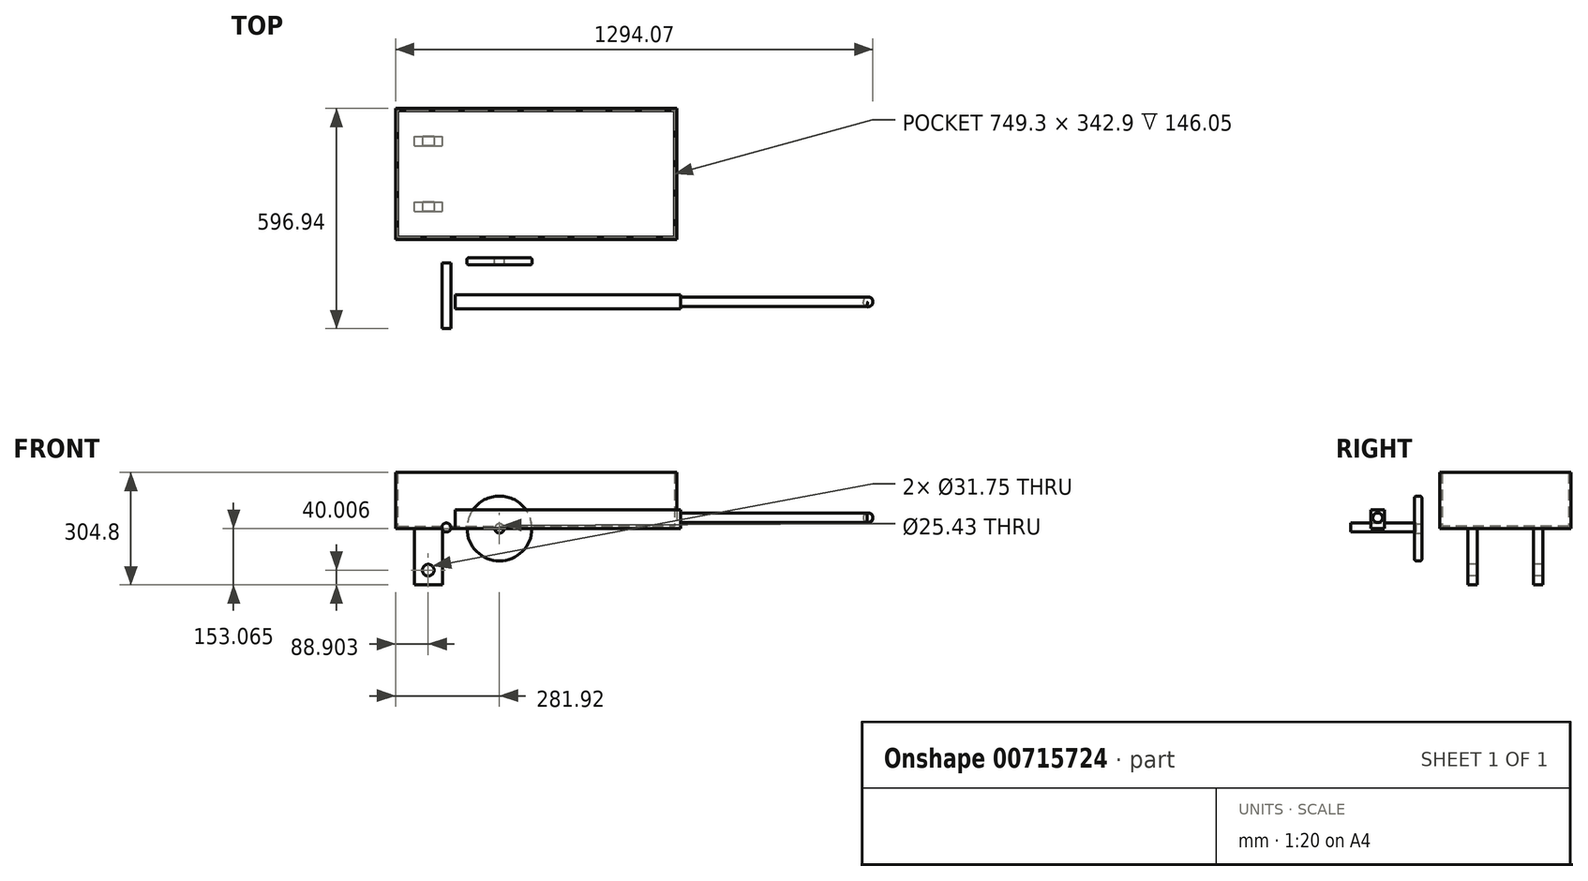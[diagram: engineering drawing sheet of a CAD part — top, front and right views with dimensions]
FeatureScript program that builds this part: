
annotation { "Feature Type Name" : "Feature", "Feature Type Description" : "" }
export const myFeature = defineFeature(function(context is Context, id is Id, definition is map)
    precondition{}
    {
        {
            var Q0;
            Q0=qCreatedBy(makeId("Top.planeOp"),FACE);
            var sketch = newSketch(context, id + "F0", { "sketchPlane" : qUnion([Q0])});
            skLineSegment(sketch, "E0.bottom", {"start": v(0, -5.26) * mm, "end": v(75.35, -5.26) * mm});
            skLineSegment(sketch, "E0.top", {"start": v(0, 14.29) * mm, "end": v(75.35, 14.29) * mm});
            skLineSegment(sketch, "E0.left", {"start": v(0, -5.26) * mm, "end": v(0, 14.29) * mm});
            skLineSegment(sketch, "E0.right", {"start": v(75.35, -5.26) * mm, "end": v(75.35, 14.29) * mm});
            skArc(sketch, "E1", {"start": v(75.35, -5.26) * mm, "mid": v(85.12, 4.51) * mm, "end": v(75.35, 14.29) * mm});
            skSolve(sketch);
        }
        {
            var Q0;
            Q0=qCreatedBy(makeId("Front.planeOp"),FACE);
            var sketch = newSketch(context, id + "F1", { "sketchPlane" : qUnion([Q0])});
            skCircle(sketch, "E2", {"center": v(-12.7, 0.66) * mm, "radius": 12.72 * mm});
            skPoint(sketch, "E2.first.point", {"position": v(0, 0) * mm});
            skPoint(sketch, "E2.second.point", {"position": v(-25.4, 0) * mm});
            skPoint(sketch, "E2.third.point", {"position": v(-23.5, -6.04) * mm});
            skSolve(sketch);
        }
        {
            var Q0;
            Q0=makeQuery(id+"F0.imprint","IMPRINT",FACE,{"disambiguationData":[TD([[makeQuery(id+"F0.imprint","IMPRINT",EDGE,{"derivedFrom":sQuery(id+"F0.wireOp",EDGE,"E0.bottom")}),1.0]])]});
            var Q1;
            Q1=sQuery(id+"F1.wireOp",EDGE,"E2");
            revolve(context, id + "F2", {"surfaceOperationType" : NewSurfaceOperationType.NEW, "entities" : qUnion([Q0]), "axis" : qUnion([Q1]), "revolveType" : RevolveType.FULL});
        }
        {
            var Q0;
            Q0=makeQuery(id+"F2.opRevolve","SWEPT_EDGE",EDGE,{"disambiguationData":[OSD([sQuery(id+"F0.wireOp",EDGE,"E0.top"),sQuery(id+"F0.wireOp",EDGE,"E0.right"),sQuery(id+"F0.wireOp",EDGE,"E1")])]});
            var Q1;
            Q1=makeQuery(id+"F2.opRevolve","SWEPT_EDGE",EDGE,{"disambiguationData":[OSD([sQuery(id+"F0.wireOp",EDGE,"E0.bottom"),sQuery(id+"F0.wireOp",EDGE,"E0.right"),sQuery(id+"F0.wireOp",EDGE,"E1")])]});
            fillet(context, id + "F3", {"entities" : qUnion([Q0, Q1]), "radius" : 5.08 * mm, "tangentPropagation" : true, "allowEdgeOverflow" : false});
        }
        {
            var Q0;
            Q0=qCreatedBy(makeId("Front.planeOp"),FACE);
            var sketch = newSketch(context, id + "F4", { "sketchPlane" : qUnion([Q0])});
            skCircle(sketch, "E3", {"center": v(-156.6, 3.33) * mm, "radius": 12.2 * mm});
            skSolve(sketch);
        }
        {
            var Q0;
            Q0=makeQuery(id+"F4.imprint","IMPRINT",FACE,{"disambiguationData":[TD([[makeQuery(id+"F4.imprint","IMPRINT",EDGE,{"derivedFrom":sQuery(id+"F4.wireOp",EDGE,"E3")}),1.0]])]});
            extrude(context, id + "F5", {"entities" : qUnion([Q0]), "depth" : 177.8 * mm, "offsetDistance" : 25.4 * mm});
        }
        {
            var Q0;
            Q0=qCreatedBy(makeId("Top.planeOp"),FACE);
            var sketch = newSketch(context, id + "F6", { "sketchPlane" : qUnion([Q0])});
            skLineSegment(sketch, "E4.bottom", {"start": v(-89.13, -56.6) * mm, "end": v(92.8, -56.6) * mm});
            skLineSegment(sketch, "E4.top", {"start": v(-89.13, -137.08) * mm, "end": v(92.8, -137.08) * mm});
            skLineSegment(sketch, "E4.left", {"start": v(-89.13, -56.6) * mm, "end": v(-89.13, -137.08) * mm});
            skLineSegment(sketch, "E4.right", {"start": v(92.8, -56.6) * mm, "end": v(92.8, -137.08) * mm});
            skLineSegment(sketch, "E5.bottom", {"start": v(-294.62, 419.14) * mm, "end": v(467.38, 419.14) * mm});
            skLineSegment(sketch, "E5.top", {"start": v(-294.62, 63.54) * mm, "end": v(467.38, 63.54) * mm});
            skLineSegment(sketch, "E5.left", {"start": v(-294.62, 419.14) * mm, "end": v(-294.62, 63.54) * mm});
            skLineSegment(sketch, "E5.right", {"start": v(467.38, 419.14) * mm, "end": v(467.38, 63.54) * mm});
            skSolve(sketch);
        }
        {
            var Q0;
            Q0=makeQuery(id+"F6.imprint","IMPRINT",FACE,{"disambiguationData":[TD([[makeQuery(id+"F6.imprint","IMPRINT",EDGE,{"derivedFrom":sQuery(id+"F6.wireOp",EDGE,"E5.bottom")}),-1.0]])]});
            extrude(context, id + "F7", {"entities" : qUnion([Q0]), "depth" : 152.4 * mm, "offsetDistance" : 25.4 * mm});
        }
        {
            var Q0;
            Q0=makeQuery(id+"F7.opExtrude","CAP_FACE",FACE,{"disambiguationData":[OSD([sQuery(id+"F6.wireOp",EDGE,"E5.bottom"),sQuery(id+"F6.wireOp",EDGE,"E5.top"),sQuery(id+"F6.wireOp",EDGE,"E5.left"),sQuery(id+"F6.wireOp",EDGE,"E5.right")])],"isStart":false});
            shell(context, id + "F8", {"entities" : qUnion([Q0]), "thickness" : 6.35 * mm});
        }
        {
            var Q0;
            Q0=makeQuery(id+"F7.opExtrude","CAP_FACE",FACE,{"disambiguationData":[OSD([sQuery(id+"F6.wireOp",EDGE,"E5.bottom"),sQuery(id+"F6.wireOp",EDGE,"E5.top"),sQuery(id+"F6.wireOp",EDGE,"E5.left"),sQuery(id+"F6.wireOp",EDGE,"E5.right")])],"isStart":true});
            var sketch = newSketch(context, id + "F9", { "sketchPlane" : qUnion([Q0])});
            skLineSegment(sketch, "E6.bottom", {"start": v(-243.82, -139.74) * mm, "end": v(-167.62, -139.74) * mm});
            skLineSegment(sketch, "E6.top", {"start": v(-243.82, -165.14) * mm, "end": v(-167.62, -165.14) * mm});
            skLineSegment(sketch, "E6.left", {"start": v(-243.82, -139.74) * mm, "end": v(-243.82, -165.14) * mm});
            skLineSegment(sketch, "E6.right", {"start": v(-167.62, -139.74) * mm, "end": v(-167.62, -165.14) * mm});
            skLineSegment(sketch, "E7.bottom", {"start": v(-243.82, -317.54) * mm, "end": v(-167.62, -317.54) * mm});
            skLineSegment(sketch, "E7.top", {"start": v(-243.82, -342.94) * mm, "end": v(-167.62, -342.94) * mm});
            skLineSegment(sketch, "E7.left", {"start": v(-243.82, -317.54) * mm, "end": v(-243.82, -342.94) * mm});
            skLineSegment(sketch, "E7.right", {"start": v(-167.62, -317.54) * mm, "end": v(-167.62, -342.94) * mm});
            skSolve(sketch);
        }
        {
            var Q0;
            Q0=makeQuery(id+"F9.imprint","IMPRINT",FACE,{"disambiguationData":[TD([[makeQuery(id+"F9.imprint","IMPRINT",EDGE,{"derivedFrom":sQuery(id+"F9.wireOp",EDGE,"E6.bottom")}),-1.0]])]});
            var Q1;
            Q1=makeQuery(id+"F9.imprint","IMPRINT",FACE,{"disambiguationData":[TD([[makeQuery(id+"F9.imprint","IMPRINT",EDGE,{"derivedFrom":sQuery(id+"F9.wireOp",EDGE,"E7.bottom")}),-1.0]])]});
            extrude(context, id + "F10", {"entities" : qUnion([Q0, Q1]), "operationType" : NewBodyOperationType.ADD, "depth" : 152.4 * mm, "offsetDistance" : 25.4 * mm});
        }
        {
            var Q0;
            Q0=makeQuery(id+"F10.opExtrude","SWEPT_FACE",FACE,{"disambiguationData":[OSD([sQuery(id+"F9.wireOp",EDGE,"E6.bottom")])]});
            var sketch = newSketch(context, id + "F11", { "sketchPlane" : qUnion([Q0])});
            skCircle(sketch, "E8", {"center": v(-205.72, -112.4) * mm, "radius": 15.88 * mm});
            skPoint(sketch, "E8.centerSnap0", {"position": v(-205.72, -152.4) * mm});
            skSolve(sketch);
        }
        {
            var Q0;
            Q0=makeQuery(id+"F11.imprint","IMPRINT",FACE,{"disambiguationData":[TD([[makeQuery(id+"F11.imprint","IMPRINT",EDGE,{"derivedFrom":sQuery(id+"F11.wireOp",EDGE,"E8")}),1.0]])]});
            extrude(context, id + "F12", {"entities" : qUnion([Q0]), "operationType" : NewBodyOperationType.REMOVE, "endBound" : BoundingType.THROUGH_ALL, "oppositeDirection" : true, "depth" : 203.2 * mm, "offsetDistance" : 25.4 * mm});
        }
        {
            var Q0;
            Q0=qCreatedBy(makeId("Top.planeOp"),FACE);
            var sketch = newSketch(context, id + "F13", { "sketchPlane" : qUnion([Q0])});
            skLineSegment(sketch, "E9.bottom", {"start": v(478.12, -123.8) * mm, "end": v(-132.17, -123.8) * mm});
            skLineSegment(sketch, "E9.top", {"start": v(478.12, -86.1) * mm, "end": v(-132.17, -86.1) * mm});
            skLineSegment(sketch, "E9.left", {"start": v(478.12, -123.8) * mm, "end": v(478.12, -86.1) * mm});
            skLineSegment(sketch, "E9.right", {"start": v(-132.17, -123.8) * mm, "end": v(-132.17, -86.1) * mm});
            skPoint(sketch, "E9.middle", {"position": v(172.98, -104.95) * mm});
            skSolve(sketch);
        }
        {
            var Q0;
            Q0=makeQuery(id+"F13.imprint","IMPRINT",FACE,{"disambiguationData":[TD([[makeQuery(id+"F13.imprint","IMPRINT",EDGE,{"derivedFrom":sQuery(id+"F13.wireOp",EDGE,"E9.bottom")}),-1.0]])]});
            extrude(context, id + "F14", {"entities" : qUnion([Q0]), "depth" : 50.8 * mm, "offsetDistance" : 25.4 * mm});
        }
        {
            var Q0;
            Q0=makeQuery(id+"F14.opExtrude","SWEPT_FACE",FACE,{"disambiguationData":[OSD([sQuery(id+"F13.wireOp",EDGE,"E9.left")])]});
            var sketch = newSketch(context, id + "F15", { "sketchPlane" : qUnion([Q0])});
            skCircle(sketch, "E10", {"center": v(-104.95, 29.81) * mm, "radius": 13.19 * mm});
            skPoint(sketch, "E10.centerSnap0", {"position": v(-104.95, 0) * mm});
            skSolve(sketch);
        }
        {
            var Q0;
            Q0 = qSketchRegion(id + "F15", true);
            extrude(context, id + "F16", {"entities" : qUnion([Q0]), "operationType" : NewBodyOperationType.ADD, "depth" : 508 * mm, "offsetDistance" : 25.4 * mm});
        }
        {
            var Q0;
            Q0=makeQuery(id+"F16.opExtrude","CAP_FACE",FACE,{"disambiguationData":[OSD([sQuery(id+"F15.wireOp",EDGE,"E10")])],"isStart":false});
            var sketch = newSketch(context, id + "F17", { "sketchPlane" : qUnion([Q0])});
            skLineSegment(sketch, "E11", {"start": v(-105.7, 42.98) * mm, "end": v(-104.5, 16.63) * mm});
            skSolve(sketch);
        }
        {
            var Q0;
            {var subQ0=sQuery(id+"F17.wireOp",EDGE,"E11");Q0=makeQuery(id+"F17.imprint","IMPRINT",FACE,{"disambiguationData":[TD([[makeQuery(id+"F17.imprint","IMPRINT",EDGE,{"derivedFrom":subQ0}),1.0]])]});}
            var Q1;
            Q1=sQuery(id+"F17.wireOp",EDGE,"E11");
            revolve(context, id + "F18", {"operationType" : NewBodyOperationType.ADD, "surfaceOperationType" : NewSurfaceOperationType.NEW, "entities" : qUnion([Q0]), "axis" : qUnion([Q1]), "revolveType" : RevolveType.FULL});
        }
    });
